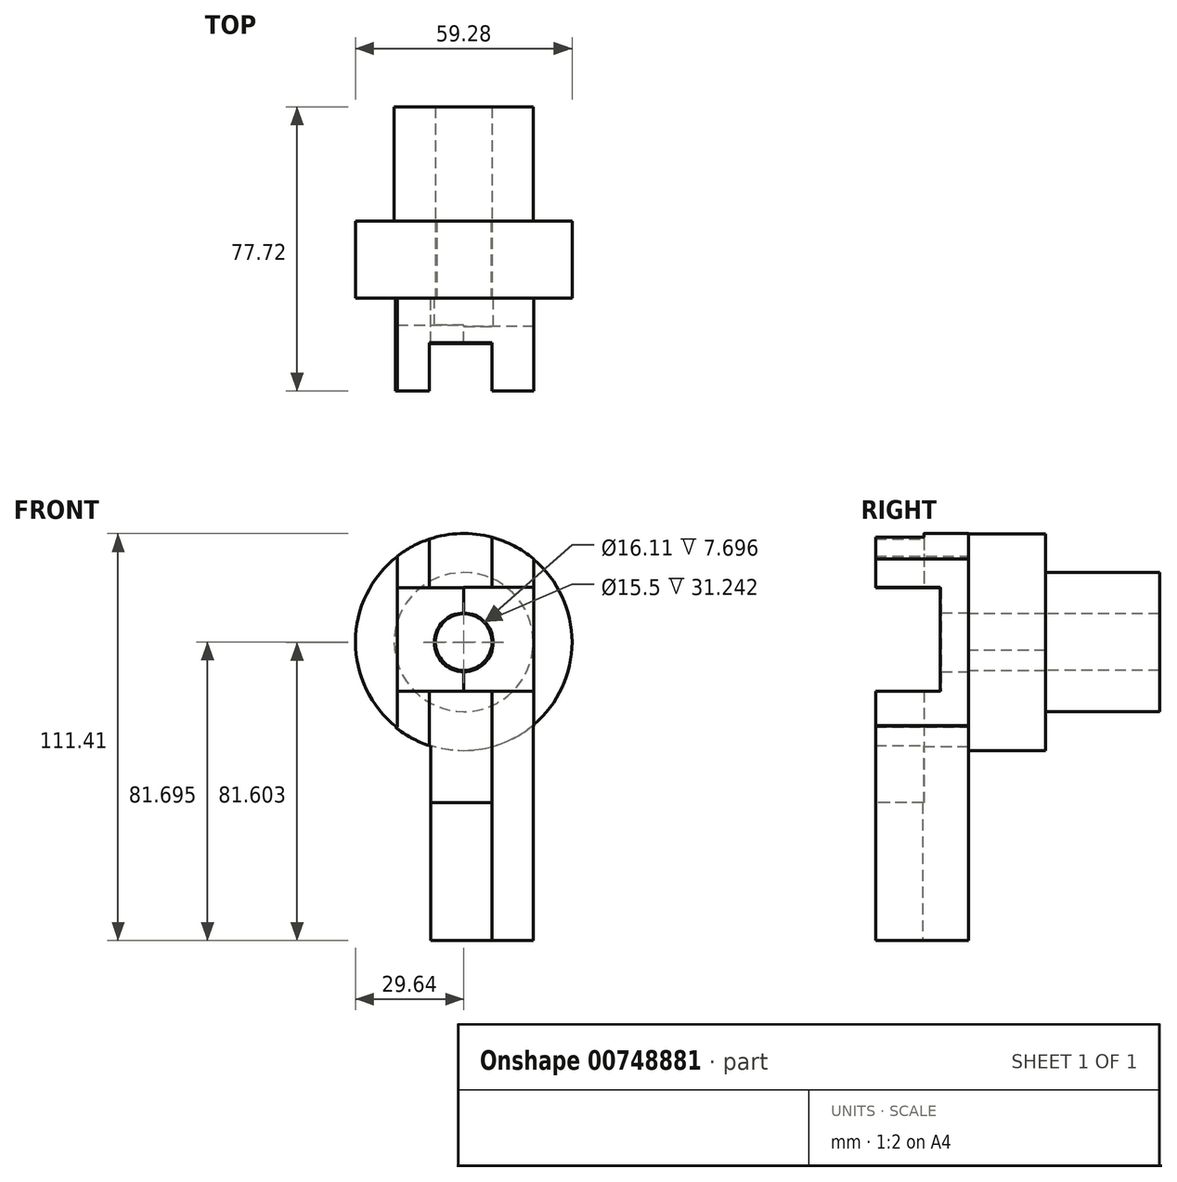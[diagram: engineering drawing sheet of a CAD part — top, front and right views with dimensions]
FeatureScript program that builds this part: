
annotation { "Feature Type Name" : "Feature", "Feature Type Description" : "" }
export const myFeature = defineFeature(function(context is Context, id is Id, definition is map)
    precondition{}
    {
        {
            var Q0;
            Q0=qCreatedBy(makeId("Front.planeOp"),FACE);
            var sketch = newSketch(context, id + "F0", { "sketchPlane" : qUnion([Q0])});
            skCircle(sketch, "E0", {"center": v(0, 43.85) * mm, "radius": 8.05 * mm});
            skCircle(sketch, "E1", {"center": v(0, 43.85) * mm, "radius": 29.8 * mm});
            skLineSegment(sketch, "E2", {"start": v(-18.34, 67.35) * mm, "end": v(-18.34, -37.75) * mm});
            skLineSegment(sketch, "E3", {"start": v(-18.34, -37.75) * mm, "end": v(19.02, -37.75) * mm});
            skLineSegment(sketch, "E4", {"start": v(19.02, -37.75) * mm, "end": v(19.02, 66.8) * mm});
            skLineSegment(sketch, "E5", {"start": v(-18.34, 28.24) * mm, "end": v(19.02, 28.24) * mm});
            skCircle(sketch, "E6", {"center": v(0.15, 43.85) * mm, "radius": 15.43 * mm});
            skLineSegment(sketch, "E7", {"start": v(-18.34, 59.6) * mm, "end": v(19.02, 59.6) * mm});
            skLineSegment(sketch, "E8", {"start": v(-9, 72.26) * mm, "end": v(-9, 59.6) * mm});
            skLineSegment(sketch, "E9", {"start": v(-9, 28.24) * mm, "end": v(-9, -37.75) * mm});
            skLineSegment(sketch, "E10", {"start": v(9.25, 72.67) * mm, "end": v(9.25, 59.6) * mm});
            skLineSegment(sketch, "E11", {"start": v(9.25, 28.52) * mm, "end": v(9.25, -37.99) * mm});
            skSolve(sketch);
        }
        {
            var Q0;
            {var subQ0=sQuery(id+"F0.wireOp",EDGE,"E2");var subQ1=sQuery(id+"F0.wireOp",EDGE,"E1");var subQ2=makeQuery(id+"F0.imprint","INTERSECT",VERTEX,{"disambiguationData":[OD(1.0)],"derivedFrom":[subQ1,subQ0]});Q0=makeQuery(id+"F0.imprint","IMPRINT",FACE,{"disambiguationData":[TD([[makeQuery(id+"F0.imprint","IMPRINT",EDGE,{"disambiguationData":[TD([[subQ2,-1.0]])],"derivedFrom":subQ1}),-1.0]])]});}
            var Q1;
            {var subQ0=sQuery(id+"F0.wireOp",EDGE,"E4");var subQ1=sQuery(id+"F0.wireOp",EDGE,"E1");var subQ2=makeQuery(id+"F0.imprint","INTERSECT",VERTEX,{"disambiguationData":[OD(1.0)],"derivedFrom":[subQ1,subQ0]});Q1=makeQuery(id+"F0.imprint","IMPRINT",FACE,{"disambiguationData":[TD([[makeQuery(id+"F0.imprint","IMPRINT",EDGE,{"disambiguationData":[TD([[subQ2,1.0]])],"derivedFrom":subQ1}),-1.0]])]});}
            var Q2;
            {var subQ0=sQuery(id+"F0.wireOp",EDGE,"E2");var subQ1=sQuery(id+"F0.wireOp",EDGE,"E1");var subQ2=makeQuery(id+"F0.imprint","INTERSECT",VERTEX,{"disambiguationData":[OD(0.0)],"derivedFrom":[subQ1,subQ0]});Q2=makeQuery(id+"F0.imprint","IMPRINT",FACE,{"disambiguationData":[TD([[makeQuery(id+"F0.imprint","IMPRINT",EDGE,{"disambiguationData":[TD([[subQ2,-1.0]])],"derivedFrom":subQ1}),1.0]])]});}
            var Q3;
            {var subQ0=sQuery(id+"F0.wireOp",EDGE,"E9");var subQ1=sQuery(id+"F0.wireOp",EDGE,"E1");var subQ2=makeQuery(id+"F0.imprint","INTERSECT",VERTEX,{"derivedFrom":[subQ1,subQ0]});Q3=makeQuery(id+"F0.imprint","IMPRINT",FACE,{"disambiguationData":[TD([[makeQuery(id+"F0.imprint","IMPRINT",EDGE,{"disambiguationData":[TD([[subQ2,-1.0]])],"derivedFrom":subQ1}),-1.0]])]});}
            var Q4;
            {var subQ0=sQuery(id+"F0.wireOp",EDGE,"E4");var subQ1=sQuery(id+"F0.wireOp",EDGE,"E1");var subQ2=makeQuery(id+"F0.imprint","INTERSECT",VERTEX,{"disambiguationData":[OD(0.0)],"derivedFrom":[subQ1,subQ0]});Q4=makeQuery(id+"F0.imprint","IMPRINT",FACE,{"disambiguationData":[TD([[makeQuery(id+"F0.imprint","IMPRINT",EDGE,{"disambiguationData":[TD([[subQ2,1.0]])],"derivedFrom":subQ1}),1.0]])]});}
            var Q5;
            {var subQ0=sQuery(id+"F0.wireOp",EDGE,"E2");var subQ1=sQuery(id+"F0.wireOp",EDGE,"E1");var subQ2=makeQuery(id+"F0.imprint","INTERSECT",VERTEX,{"disambiguationData":[OD(1.0)],"derivedFrom":[subQ1,subQ0]});Q5=makeQuery(id+"F0.imprint","IMPRINT",FACE,{"disambiguationData":[TD([[makeQuery(id+"F0.imprint","IMPRINT",EDGE,{"disambiguationData":[TD([[subQ2,-1.0]])],"derivedFrom":subQ1}),1.0]])]});}
            var Q6;
            {var subQ0=sQuery(id+"F0.wireOp",EDGE,"E4");var subQ1=sQuery(id+"F0.wireOp",EDGE,"E1");var subQ2=makeQuery(id+"F0.imprint","INTERSECT",VERTEX,{"disambiguationData":[OD(1.0)],"derivedFrom":[subQ1,subQ0]});Q6=makeQuery(id+"F0.imprint","IMPRINT",FACE,{"disambiguationData":[TD([[makeQuery(id+"F0.imprint","IMPRINT",EDGE,{"disambiguationData":[TD([[subQ2,1.0]])],"derivedFrom":subQ1}),1.0]])]});}
            var Q7;
            {var subQ3=sQuery(id+"F0.wireOp",EDGE,"E8");Q7=makeQuery(id+"F0.imprint","IMPRINT",FACE,{"disambiguationData":[TD([[makeQuery(id+"F0.imprint","IMPRINT",EDGE,{"derivedFrom":subQ3}),-1.0]])]});}
            var Q8;
            {var subQ0=sQuery(id+"F0.wireOp",EDGE,"E4");var subQ1=sQuery(id+"F0.wireOp",EDGE,"E1");var subQ2=makeQuery(id+"F0.imprint","INTERSECT",VERTEX,{"disambiguationData":[OD(0.0)],"derivedFrom":[subQ1,subQ0]});Q8=makeQuery(id+"F0.imprint","IMPRINT",FACE,{"disambiguationData":[TD([[makeQuery(id+"F0.imprint","IMPRINT",EDGE,{"disambiguationData":[TD([[subQ2,-1.0]])],"derivedFrom":subQ1}),1.0]])]});}
            var Q9;
            Q9=makeQuery(id+"F0.imprint","IMPRINT",FACE,{"disambiguationData":[TD([[makeQuery(id+"F0.imprint","IMPRINT",EDGE,{"derivedFrom":sQuery(id+"F0.wireOp",EDGE,"E0")}),-1.0]])]});
            var Q10;
            {var subQ0=sQuery(id+"F0.wireOp",EDGE,"E8");Q10=makeQuery(id+"F0.imprint","IMPRINT",FACE,{"disambiguationData":[TD([[makeQuery(id+"F0.imprint","IMPRINT",EDGE,{"derivedFrom":subQ0}),1.0]])]});}
            var Q11;
            {var subQ0=sQuery(id+"F0.wireOp",EDGE,"E9");var subQ1=sQuery(id+"F0.wireOp",EDGE,"E1");var subQ2=makeQuery(id+"F0.imprint","INTERSECT",VERTEX,{"derivedFrom":[subQ1,subQ0]});Q11=makeQuery(id+"F0.imprint","IMPRINT",FACE,{"disambiguationData":[TD([[makeQuery(id+"F0.imprint","IMPRINT",EDGE,{"disambiguationData":[TD([[subQ2,-1.0]])],"derivedFrom":subQ1}),1.0]])]});}
            var Q12;
            Q12=makeQuery(id+"F0.imprint","IMPRINT",FACE,{"disambiguationData":[TD([[makeQuery(id+"F0.imprint","IMPRINT",EDGE,{"derivedFrom":sQuery(id+"F0.wireOp",EDGE,"E6")}),-1.0]])]});
            extrude(context, id + "F1", {"entities" : qUnion([Q0, Q1, Q2, Q3, Q4, Q5, Q6, Q7, Q8, Q9, Q10, Q11, Q12]), "depth" : 25.4 * mm, "offsetDistance" : 25.4 * mm});
        }
        {
            var Q0;
            Q0=qCreatedBy(makeId("Top.planeOp"),FACE);
            var sketch = newSketch(context, id + "F2", { "sketchPlane" : qUnion([Q0])});
            skLineSegment(sketch, "E12", {"start": v(-9.44, -26.43) * mm, "end": v(-9.44, -12.49) * mm});
            skLineSegment(sketch, "E13", {"start": v(-9.44, -12.49) * mm, "end": v(7.7, -12.49) * mm});
            skLineSegment(sketch, "E14", {"start": v(7.7, -12.49) * mm, "end": v(7.7, -26.43) * mm});
            skLineSegment(sketch, "E15", {"start": v(7.7, -26.43) * mm, "end": v(-9.44, -26.43) * mm});
            skSolve(sketch);
        }
        {
            var Q0;
            Q0 = qSketchRegion(id + "F2", true);
            extrude(context, id + "F3", {"entities" : qUnion([Q0]), "operationType" : NewBodyOperationType.REMOVE, "oppositeDirection" : true, "depth" : 52.07 * mm, "offsetDistance" : 25.4 * mm});
        }
        {
            var Q0;
            Q0=qCreatedBy(makeId("Top.planeOp"),FACE);
            var sketch = newSketch(context, id + "F4", { "sketchPlane" : qUnion([Q0])});
            skLineSegment(sketch, "E16", {"start": v(-9.44, -26.98) * mm, "end": v(-9.44, -12.2) * mm});
            skLineSegment(sketch, "E17", {"start": v(-9.44, -12.2) * mm, "end": v(7.72, -12.2) * mm});
            skLineSegment(sketch, "E18", {"start": v(7.72, -12.2) * mm, "end": v(7.72, -26.98) * mm});
            skLineSegment(sketch, "E19", {"start": v(7.72, -26.98) * mm, "end": v(-9.44, -26.98) * mm});
            skSolve(sketch);
        }
        {
            var Q0;
            Q0 = qSketchRegion(id + "F4", true);
            extrude(context, id + "F5", {"entities" : qUnion([Q0]), "operationType" : NewBodyOperationType.REMOVE, "depth" : 100.08 * mm, "offsetDistance" : 25.4 * mm});
        }
        {
            var Q0;
            Q0=qCreatedBy(makeId("Front.planeOp"),FACE);
            var sketch = newSketch(context, id + "F6", { "sketchPlane" : qUnion([Q0])});
            skCircle(sketch, "E20", {"center": v(0, 43.85) * mm, "radius": 30.12 * mm});
            skCircle(sketch, "E21", {"center": v(0, 43.85) * mm, "radius": 7.75 * mm});
            skSolve(sketch);
        }
        {
            var Q0;
            Q0=qCreatedBy(makeId("Right.planeOp"),FACE);
            var sketch = newSketch(context, id + "F7", { "sketchPlane" : qUnion([Q0])});
            skLineSegment(sketch, "E22", {"start": v(-7.7, 30.5) * mm, "end": v(-28.03, 30.5) * mm});
            skLineSegment(sketch, "E23", {"start": v(-28.03, 30.5) * mm, "end": v(-28.03, 58.95) * mm});
            skLineSegment(sketch, "E24", {"start": v(-28.03, 58.95) * mm, "end": v(-7.7, 58.95) * mm});
            skLineSegment(sketch, "E25", {"start": v(-7.7, 58.95) * mm, "end": v(-7.7, 30.5) * mm});
            skSolve(sketch);
        }
        {
            var Q0;
            Q0 = qSketchRegion(id + "F7", true);
            extrude(context, id + "F8", {"entities" : qUnion([Q0]), "operationType" : NewBodyOperationType.REMOVE, "depth" : 57.66 * mm, "offsetDistance" : 25.4 * mm});
        }
        {
            var Q0;
            Q0=qCreatedBy(makeId("Right.planeOp"),FACE);
            var sketch = newSketch(context, id + "F9", { "sketchPlane" : qUnion([Q0])});
            skLineSegment(sketch, "E26", {"start": v(-27.74, 58.82) * mm, "end": v(-27.74, 30.5) * mm});
            skLineSegment(sketch, "E27", {"start": v(-27.74, 30.5) * mm, "end": v(-7.4, 30.5) * mm});
            skLineSegment(sketch, "E28", {"start": v(-7.4, 30.5) * mm, "end": v(-7.4, 58.82) * mm});
            skLineSegment(sketch, "E29", {"start": v(-7.4, 58.82) * mm, "end": v(-27.74, 58.82) * mm});
            skSolve(sketch);
        }
        {
            var Q0;
            Q0 = qSketchRegion(id + "F9", true);
            extrude(context, id + "F10", {"entities" : qUnion([Q0]), "operationType" : NewBodyOperationType.REMOVE, "oppositeDirection" : true, "depth" : 54.6 * mm, "offsetDistance" : 25.4 * mm});
        }
        {
            var Q0;
            Q0=qCreatedBy(makeId("Front.planeOp"),FACE);
            var sketch = newSketch(context, id + "F11", { "sketchPlane" : qUnion([Q0])});
            skLineSegment(sketch, "E30", {"start": v(19.22, 69.31) * mm, "end": v(19.22, 20.48) * mm});
            skLineSegment(sketch, "E31", {"start": v(19.22, 20.48) * mm, "end": v(39.07, 20.48) * mm});
            skLineSegment(sketch, "E32", {"start": v(39.07, 20.48) * mm, "end": v(39.07, 69.31) * mm});
            skLineSegment(sketch, "E33", {"start": v(39.07, 69.31) * mm, "end": v(19.22, 69.31) * mm});
            skLineSegment(sketch, "E34", {"start": v(-18.2, 69.31) * mm, "end": v(-18.2, 20.66) * mm});
            skLineSegment(sketch, "E35", {"start": v(-18.2, 20.66) * mm, "end": v(-38.19, 20.66) * mm});
            skLineSegment(sketch, "E36", {"start": v(-38.19, 20.66) * mm, "end": v(-38.19, 69.31) * mm});
            skLineSegment(sketch, "E37", {"start": v(-38.19, 69.31) * mm, "end": v(-18.2, 69.31) * mm});
            skSolve(sketch);
        }
        {
            var Q0;
            Q0 = qSketchRegion(id + "F11", true);
            extrude(context, id + "F12", {"entities" : qUnion([Q0]), "operationType" : NewBodyOperationType.REMOVE, "depth" : 44.7 * mm, "offsetDistance" : 25.4 * mm});
        }
        {
            var Q0;
            Q0=makeQuery(id+"F6.imprint","IMPRINT",FACE,{"disambiguationData":[TD([[makeQuery(id+"F6.imprint","IMPRINT",EDGE,{"derivedFrom":sQuery(id+"F6.wireOp",EDGE,"E20")}),1.0]])]});
            var sketch = newSketch(context, id + "F13", { "sketchPlane" : qUnion([Q0])});
            skCircle(sketch, "E38", {"center": v(0, 43.94) * mm, "radius": 29.64 * mm});
            skCircle(sketch, "E39", {"center": v(0, 43.94) * mm, "radius": 7.77 * mm});
            skCircle(sketch, "E40", {"center": v(0, 43.94) * mm, "radius": 17.94 * mm});
            skSolve(sketch);
        }
        {
            var Q0;
            Q0=makeQuery(id+"F13.imprint","IMPRINT",FACE,{"disambiguationData":[TD([[makeQuery(id+"F13.imprint","IMPRINT",EDGE,{"derivedFrom":sQuery(id+"F13.wireOp",EDGE,"E38")}),1.0]])]});
            var Q1;
            Q1=makeQuery(id+"F13.imprint","IMPRINT",FACE,{"disambiguationData":[TD([[makeQuery(id+"F13.imprint","IMPRINT",EDGE,{"derivedFrom":sQuery(id+"F13.wireOp",EDGE,"E40")}),1.0]])]});
            extrude(context, id + "F14", {"entities" : qUnion([Q0, Q1]), "operationType" : NewBodyOperationType.ADD, "oppositeDirection" : true, "depth" : 21.08 * mm, "offsetDistance" : 25.4 * mm});
        }
        {
            var Q0;
            Q0=makeQuery(id+"F14.opExtrude","CAP_FACE",FACE,{"disambiguationData":[OSD([sQuery(id+"F6.wireOp",EDGE,"E21"),sQuery(id+"F13.wireOp",EDGE,"E38"),sQuery(id+"F13.wireOp",EDGE,"E39")])],"isStart":false});
            var sketch = newSketch(context, id + "F15", { "sketchPlane" : qUnion([Q0])});
            skCircle(sketch, "E41", {"center": v(0, 43.94) * mm, "radius": 7.75 * mm});
            skCircle(sketch, "E42", {"center": v(0, 43.94) * mm, "radius": 19.02 * mm});
            skSolve(sketch);
        }
        {
            var Q0;
            Q0 = qSketchRegion(id + "F15", true);
            extrude(context, id + "F16", {"entities" : qUnion([Q0]), "operationType" : NewBodyOperationType.ADD, "depth" : 31.24 * mm, "offsetDistance" : 25.4 * mm});
        }
    });
